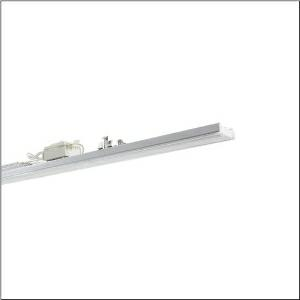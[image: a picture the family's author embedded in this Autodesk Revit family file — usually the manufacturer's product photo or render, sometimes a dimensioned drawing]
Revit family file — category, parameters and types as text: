
# Revit family: licross_21_recessed_mo_52te10dv4e5g
name_source: partatom
category: Lighting Fixtures
units: mm (PartAtom-declared; Revit-internal decimal feet)

## family parameters
Cut with Voids When Loaded = No
Host = Face
Light Source = No
Part Type = Normal
Room Calculation Point = No
Round Connector Dimension = Use Diameter
Shared = No

## types (1)
- --- (1 x LED, 14990 lm, 85.3 W, 4000K)
    Apparent Load = 85 VA
    CIE Flux Codes = 50 81 96 100 100
    Color Rendering = 80
    Color Temperature = 4000K
    Default Elevation = 1800 mm
    Description = Licross 21 Recessed MO, luminaire insert, of sheet steel, galvanised, coil coated, white, length: 2.250mm, width: 66mm, height: 67mm, LED rated luminous flux: 14.990lm, light colour: 840, SDCM (Standard Deviation of Colour Matching)MacAdam ≤ 3 SDCM (initial), control gear: DALI 2, with plug, 5-pole, with phase selection, mains connection: 220..240V, AC, 50/60Hz, rated input power: 85W, internal wiring halogen-free, primary optical cover: cover, of PMMA, light emission: direct distribution, primary light characteristic: symmetric, protection rating (complete): IP54, insulation class (complete): insulation class I (protective earthing), certification: CE, ENEC, VDE, UKCA, protection symbol: D if used in an environment with non-conductive dust loads with corresponding accessories, impact resistance: IK06, permissible ambient temperature for indoor applications: -25..+35°C, corresponds to IFS (International Featured Standards) requirements for safety and quality in the food industry, reducing of maximum allowable ambient temperature of 5°C with ceiling mounting, LABS conformity tested according to VDMA 24364:2018-05, The light source and the operating device comply with the requirements of the Ecodesign Regulation (EU) 2019/2020 and are replaceable in accordance with this regulation, packaging unit: 1 piece
    Height = 58 mm
    Lamp = 1 x LED
    Lamp Light Flux = 14990 lm
    Lamp Power = 85.3 W
    Lamp count = 1
    Length = 2250 mm
    Luminous efficacy = 176 lm/W
    Manufacturer = Siteco
    ModVariant = No
    Model = 52TE10DV4E5G
    Mounting Place = Ceiling
    Mounting Type = Pendant
    Number of Poles = 1
    OnlyDefault = Yes
    Power Factor = 1
    Product Name = Licross 21 Recessed MO
    Product group = luminaire insert | ceiling pendant
    ProductGroupID = 901
    Protection Class = Protection class I
    Protection Degree = IP 54
    RLX_Detail_Level = 1
    RLX_Emergency_Light_Flux = 0 lm
    RLX_Emergency_Type = 0
    RLX_Emergency_Type_DB = No
    RlxData = <blob elided: 29669 chars, md5=66e7b821>
    Socket = socket
    Standby Power = 0 W
    System Light Flux = 14990 lm
    System Power = 85 W
    Type Comments = factory setting: luminous flux: 100 % | dim-lin: 254 | 390 mA
    Type Image = l_1296930.jpg
    URL = http://relux.com
    VarID = @adj_127759
    Voltage = 0 V
    Weight = 0.00 kg
    Width = 66 mm

## geometry (parser evidence)
native form markers: Blend x4, Sweep x10
no freeform markers — native parametric forms only
